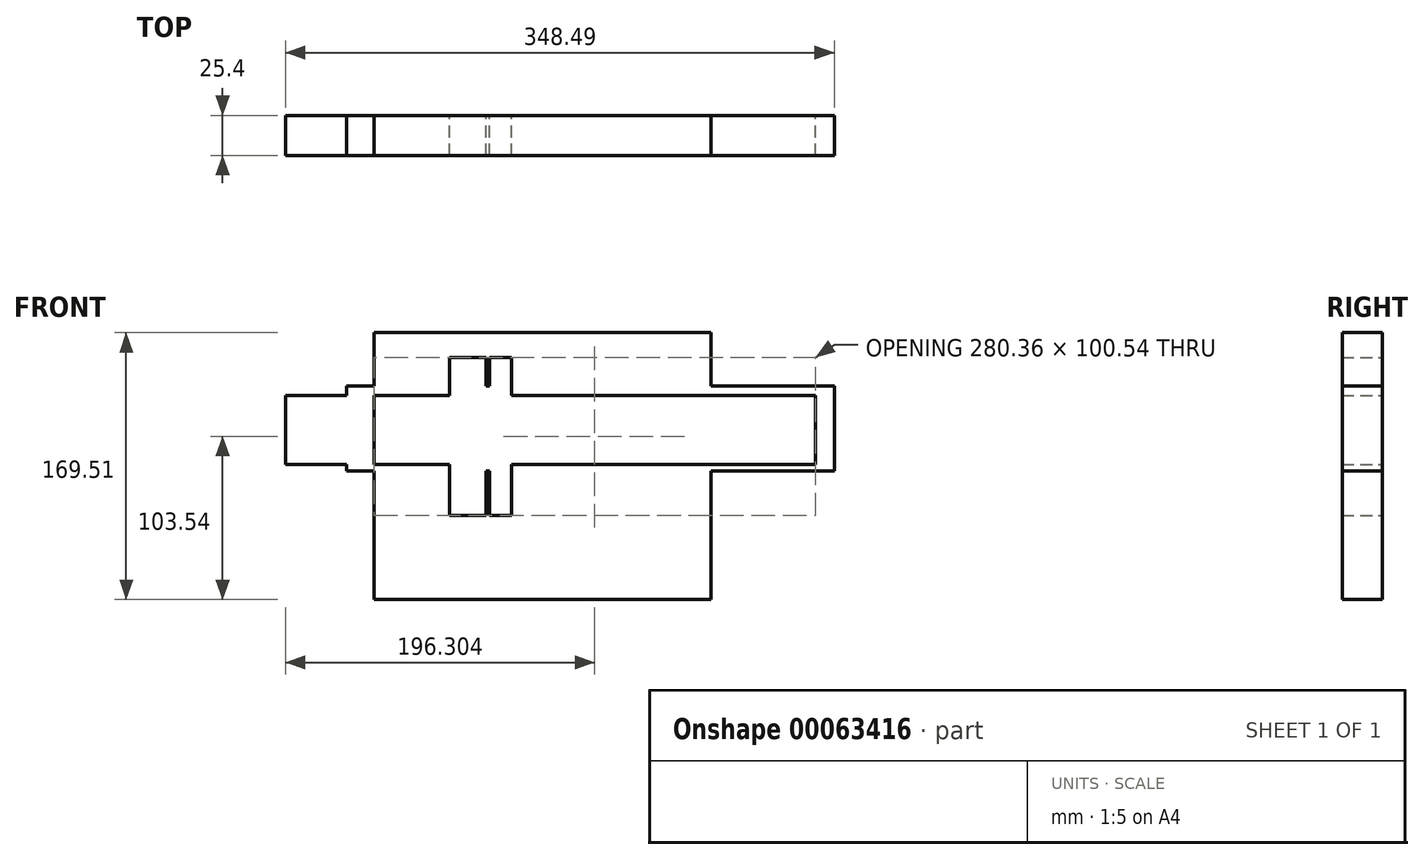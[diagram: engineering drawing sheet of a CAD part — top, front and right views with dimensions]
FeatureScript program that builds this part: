
annotation { "Feature Type Name" : "Feature", "Feature Type Description" : "" }
export const myFeature = defineFeature(function(context is Context, id is Id, definition is map)
    precondition{}
    {
        {
            var Q0;
            Q0=qCreatedBy(makeId("Front.planeOp"),FACE);
            var sketch = newSketch(context, id + "F0", { "sketchPlane" : qUnion([Q0])});
            skLineSegment(sketch, "E0.bottom", {"start": v(0, 0) * mm, "end": v(-13.93, 0) * mm});
            skLineSegment(sketch, "E0.top", {"start": v(0, 100.54) * mm, "end": v(-13.93, 100.54) * mm});
            skLineSegment(sketch, "E0.left", {"start": v(0, 0) * mm, "end": v(0, 100.54) * mm});
            skLineSegment(sketch, "E0.right", {"start": v(-13.93, 0) * mm, "end": v(-13.93, 100.54) * mm});
            skLineSegment(sketch, "E1.bottom", {"start": v(-16.24, 100.54) * mm, "end": v(-39.33, 100.54) * mm});
            skLineSegment(sketch, "E1.top", {"start": v(-16.24, 0) * mm, "end": v(-39.33, 0) * mm});
            skLineSegment(sketch, "E1.left", {"start": v(-16.24, 100.54) * mm, "end": v(-16.24, 0) * mm});
            skLineSegment(sketch, "E1.right", {"start": v(-39.33, 100.54) * mm, "end": v(-39.33, 0) * mm});
            skLineSegment(sketch, "E2.bottom", {"start": v(-87.37, 116.24) * mm, "end": v(126.72, 116.24) * mm});
            skLineSegment(sketch, "E2.top", {"start": v(-87.37, -53.27) * mm, "end": v(126.72, -53.27) * mm});
            skLineSegment(sketch, "E2.left", {"start": v(-87.37, 116.24) * mm, "end": v(-87.37, -53.27) * mm});
            skLineSegment(sketch, "E2.right", {"start": v(126.72, 116.24) * mm, "end": v(126.72, -53.27) * mm});
            skLineSegment(sketch, "E3.bottom", {"start": v(-104.92, 82.3) * mm, "end": v(205, 82.3) * mm});
            skLineSegment(sketch, "E3.top", {"start": v(-104.92, 28.49) * mm, "end": v(205, 28.49) * mm});
            skLineSegment(sketch, "E3.left", {"start": v(-104.92, 82.3) * mm, "end": v(-104.92, 28.49) * mm});
            skLineSegment(sketch, "E3.right", {"start": v(205, 82.3) * mm, "end": v(205, 28.49) * mm});
            skLineSegment(sketch, "E4.bottom", {"start": v(193, 32.41) * mm, "end": v(-143.49, 32.41) * mm});
            skLineSegment(sketch, "E4.top", {"start": v(193, 76.3) * mm, "end": v(-143.49, 76.3) * mm});
            skLineSegment(sketch, "E4.left", {"start": v(193, 32.41) * mm, "end": v(193, 76.3) * mm});
            skLineSegment(sketch, "E4.right", {"start": v(-143.49, 32.41) * mm, "end": v(-143.49, 76.3) * mm});
            skSolve(sketch);
        }
        {
            var Q0;
            Q0 = qSketchRegion(id + "F0", true);
            extrude(context, id + "F1", {"entities" : qUnion([Q0]), "depth" : 25.4 * mm});
        }
    });
